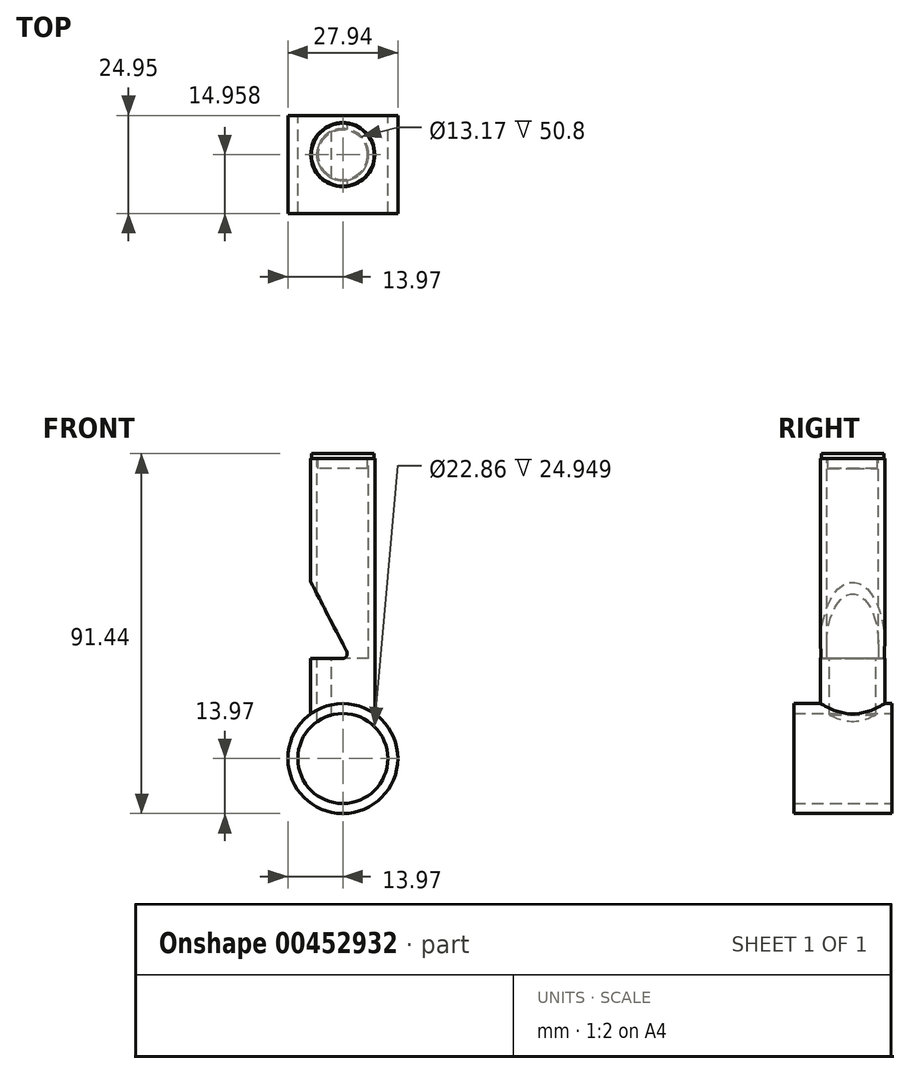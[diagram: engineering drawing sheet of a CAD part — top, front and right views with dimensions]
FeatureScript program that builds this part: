
annotation { "Feature Type Name" : "Feature", "Feature Type Description" : "" }
export const myFeature = defineFeature(function(context is Context, id is Id, definition is map)
    precondition{}
    {
        {
            var Q0;
            Q0=qCreatedBy(makeId("Front.planeOp"),FACE);
            var sketch = newSketch(context, id + "F0", { "sketchPlane" : qUnion([Q0])});
            skCircle(sketch, "E0", {"center": v(0, 0) * mm, "radius": 11.43 * mm});
            skCircle(sketch, "E1", {"center": v(0, 0) * mm, "radius": 13.97 * mm});
            skSolve(sketch);
        }
        {
            var Q0;
            Q0 = qSketchRegion(id + "F0", true);
            extrude(context, id + "F1", {"entities" : qUnion([Q0]), "depth" : 76.2 * mm});
        }
        {
            var Q0;
            Q0=qCreatedBy(makeId("Top.planeOp"),FACE);
            var sketch = newSketch(context, id + "F2", { "sketchPlane" : qUnion([Q0])});
            skCircle(sketch, "E2", {"center": v(0, -14.34) * mm, "radius": 6.59 * mm});
            skCircle(sketch, "E3", {"center": v(0, -14.34) * mm, "radius": 8.14 * mm});
            skCircle(sketch, "E4", {"center": v(0, -37.78) * mm, "radius": 6.59 * mm});
            skCircle(sketch, "E5", {"center": v(0, -37.78) * mm, "radius": 8.14 * mm});
            skCircle(sketch, "E6", {"center": v(0, -61.24) * mm, "radius": 6.59 * mm});
            skCircle(sketch, "E7", {"center": v(0, -61.24) * mm, "radius": 8.14 * mm});
            skSolve(sketch);
        }
        {
            var Q0;
            Q0 = qSketchRegion(id + "F2", true);
            var Q1;
            Q1=makeQuery(id+"F2.imprint","IMPRINT",FACE,{"disambiguationData":[TD([[makeQuery(id+"F2.imprint","IMPRINT",EDGE,{"derivedFrom":sQuery(id+"F2.wireOp",EDGE,"E6")}),1.0]])]});
            var Q2;
            Q2=makeQuery(id+"F2.imprint","IMPRINT",FACE,{"disambiguationData":[TD([[makeQuery(id+"F2.imprint","IMPRINT",EDGE,{"derivedFrom":sQuery(id+"F2.wireOp",EDGE,"E2")}),1.0]])]});
            var Q3;
            Q3=makeQuery(id+"F2.imprint","IMPRINT",FACE,{"disambiguationData":[TD([[makeQuery(id+"F2.imprint","IMPRINT",EDGE,{"derivedFrom":sQuery(id+"F2.wireOp",EDGE,"E4")}),1.0]])]});
            extrude(context, id + "F3", {"entities" : qUnion([Q0, Q1, Q2, Q3]), "operationType" : NewBodyOperationType.ADD, "depth" : 25.4 * mm});
        }
        {
            var Q0;
            Q0=makeQuery(id+"F3.opExtrude","CAP_FACE",FACE,{"disambiguationData":[OSD([sQuery(id+"F2.wireOp",EDGE,"E7")])],"isStart":false});
            var sketch = newSketch(context, id + "F4", { "sketchPlane" : qUnion([Q0])});
            skLineSegment(sketch, "E8", {"start": v(-2.92, -67.14) * mm, "end": v(-2.92, -55.34) * mm});
            skArc(sketch, "E9.0", {"start": v(-2.92, -8.51) * mm, "mid": v(-6.52, -14.38) * mm, "end": v(-2.92, -20.25) * mm});
            skArc(sketch, "E10.0", {"start": v(-2.92, -31.96) * mm, "mid": v(-6.52, -37.82) * mm, "end": v(-2.92, -43.7) * mm});
            skArc(sketch, "E11.0", {"start": v(-2.92, -55.34) * mm, "mid": v(-6.59, -61.24) * mm, "end": v(-2.92, -67.14) * mm});
            skLineSegment(sketch, "E12.trimOffspring", {"start": v(-2.92, -20.25) * mm, "end": v(-2.92, -8.51) * mm});
            skLineSegment(sketch, "E13.trimOffspring", {"start": v(-2.92, -43.7) * mm, "end": v(-2.92, -31.96) * mm});
            skSolve(sketch);
        }
        {
            var Q0;
            Q0 = qSketchRegion(id + "F4", true);
            extrude(context, id + "F5", {"entities" : qUnion([Q0]), "operationType" : NewBodyOperationType.REMOVE, "oppositeDirection" : true, "depth" : 25.4 * mm});
        }
        {
            var Q0;
            Q0=makeQuery(id+"F2.imprint","IMPRINT",FACE,{"disambiguationData":[TD([[makeQuery(id+"F2.imprint","IMPRINT",EDGE,{"derivedFrom":sQuery(id+"F2.wireOp",EDGE,"E6")}),-1.0]])]});
            var Q1;
            Q1=sQuery(id+"F2.wireOp",EDGE,"E7");
            var Q2;
            Q2=sQuery(id+"F2.wireOp",EDGE,"E6");
            extrude(context, id + "F6", {"entities" : qUnion([Q0]), "operationType" : NewBodyOperationType.ADD, "surfaceEntities" : qUnion([Q1, Q2]), "depth" : 76.2 * mm});
        }
        {
            var Q0;
            Q0=makeQuery(id+"F0.imprint","IMPRINT",FACE,{"disambiguationData":[TD([[makeQuery(id+"F0.imprint","IMPRINT",EDGE,{"derivedFrom":sQuery(id+"F0.wireOp",EDGE,"E0")}),1.0]])]});
            var Q1;
            Q1=sQuery(id+"F0.wireOp",EDGE,"E0");
            extrude(context, id + "F7", {"entities" : qUnion([Q0]), "operationType" : NewBodyOperationType.REMOVE, "surfaceEntities" : qUnion([Q1]), "depth" : 89.08 * mm});
        }
        {
            var Q0;
            Q0=qCreatedBy(makeId("Front.planeOp"),FACE);
            var sketch = newSketch(context, id + "F8", { "sketchPlane" : qUnion([Q0])});
            skLineSegment(sketch, "E14.0", {"start": v(-8.14, 25.4) * mm, "end": v(1.93, 25.4) * mm});
            skLineSegment(sketch, "E15", {"start": v(-8.14, 25.4) * mm, "end": v(-8.14, 44.89) * mm});
            skLineSegment(sketch, "E16", {"start": v(1.93, 25.4) * mm, "end": v(-8.14, 44.89) * mm});
            skPoint(sketch, "E17.orphan", {"position": v(8.14, 25.4) * mm});
            skSolve(sketch);
        }
        {
            var Q0;
            Q0 = qSketchRegion(id + "F8", true);
            extrude(context, id + "F9", {"entities" : qUnion([Q0]), "operationType" : NewBodyOperationType.REMOVE, "depth" : 93.22 * mm});
        }
        {
            var Q0;
            Q0=qCreatedBy(makeId("Right.planeOp"),FACE);
            var sketch = newSketch(context, id + "F10", { "sketchPlane" : qUnion([Q0])});
            skLineSegment(sketch, "E18.bottom", {"start": v(-51.25, -30.05) * mm, "end": v(51.25, -30.05) * mm});
            skLineSegment(sketch, "E18.top", {"start": v(-51.25, 62.5) * mm, "end": v(51.25, 62.5) * mm});
            skLineSegment(sketch, "E18.left", {"start": v(-51.25, -30.05) * mm, "end": v(-51.25, 62.5) * mm});
            skLineSegment(sketch, "E18.right", {"start": v(51.25, -30.05) * mm, "end": v(51.25, 62.5) * mm});
            skSolve(sketch);
        }
        {
            var Q0;
            Q0 = qSketchRegion(id + "F10", true);
            extrude(context, id + "F11", {"entities" : qUnion([Q0]), "operationType" : NewBodyOperationType.REMOVE, "endBound" : BoundingType.SYMMETRIC, "oppositeDirection" : true, "depth" : 76.2 * mm});
        }
        {
            var Q0;
            Q0=makeQuery(id+"F6.opExtrude","CAP_FACE",FACE,{"disambiguationData":[OSD([sQuery(id+"F2.wireOp",EDGE,"E6"),sQuery(id+"F2.wireOp",EDGE,"E7")])],"isStart":false});
            var sketch = newSketch(context, id + "F12", { "sketchPlane" : qUnion([Q0])});
            skCircle(sketch, "E19", {"center": v(0, -61.24) * mm, "radius": 6.3 * mm});
            skCircle(sketch, "E20", {"center": v(0, -61.24) * mm, "radius": 7.99 * mm});
            skSolve(sketch);
        }
        {
            var Q0;
            Q0=makeQuery(id+"F12.imprint","IMPRINT",FACE,{"disambiguationData":[TD([[makeQuery(id+"F12.imprint","IMPRINT",EDGE,{"derivedFrom":sQuery(id+"F12.wireOp",EDGE,"E19")}),1.0]])]});
            var Q1;
            Q1=sQuery(id+"F12.wireOp",EDGE,"E19");
            extrude(context, id + "F13", {"entities" : qUnion([Q0]), "surfaceEntities" : qUnion([Q1]), "oppositeDirection" : true, "depth" : 2.54 * mm});
        }
        {
            var Q0;
            Q0=makeQuery(id+"F12.imprint","IMPRINT",FACE,{"disambiguationData":[TD([[makeQuery(id+"F12.imprint","IMPRINT",EDGE,{"derivedFrom":sQuery(id+"F12.wireOp",EDGE,"E20")}),1.0]])]});
            var Q1;
            Q1=makeQuery(id+"F12.imprint","IMPRINT",FACE,{"disambiguationData":[TD([[makeQuery(id+"F12.imprint","IMPRINT",EDGE,{"derivedFrom":sQuery(id+"F12.wireOp",EDGE,"E19")}),-1.0]])]});
            var Q2;
            Q2=makeQuery(id+"F12.imprint","IMPRINT",FACE,{"disambiguationData":[TD([[makeQuery(id+"F12.imprint","IMPRINT",EDGE,{"derivedFrom":sQuery(id+"F12.wireOp",EDGE,"E19")}),1.0]])]});
            var Q3;
            Q3=sQuery(id+"F12.wireOp",EDGE,"E20");
            extrude(context, id + "F14", {"entities" : qUnion([Q0, Q1, Q2]), "surfaceEntities" : qUnion([Q3]), "depth" : 1.27 * mm});
        }
        {
            var Q0;
            Q0=makeQuery(id+"F9.boolean.opBoolean","COPY",EDGE,{"disambiguationData":[OD(0.0)],"derivedFrom":makeQuery(id+"F9.opExtrude","SWEPT_EDGE",EDGE,{"disambiguationData":[OSD([sQuery(id+"F8.wireOp",EDGE,"E14.0"),sQuery(id+"F8.wireOp",EDGE,"E16")])]})});
            var Q1;
            Q1=makeQuery(id+"F9.boolean.opBoolean","COPY",EDGE,{"disambiguationData":[OD(1.0)],"derivedFrom":makeQuery(id+"F9.opExtrude","SWEPT_EDGE",EDGE,{"disambiguationData":[OSD([sQuery(id+"F8.wireOp",EDGE,"E14.0"),sQuery(id+"F8.wireOp",EDGE,"E16")])]})});
            fillet(context, id + "F15", {"entities" : qUnion([Q0, Q1]), "radius" : 1.27 * mm, "tangentPropagation" : true, "allowEdgeOverflow" : false});
        }
    });
